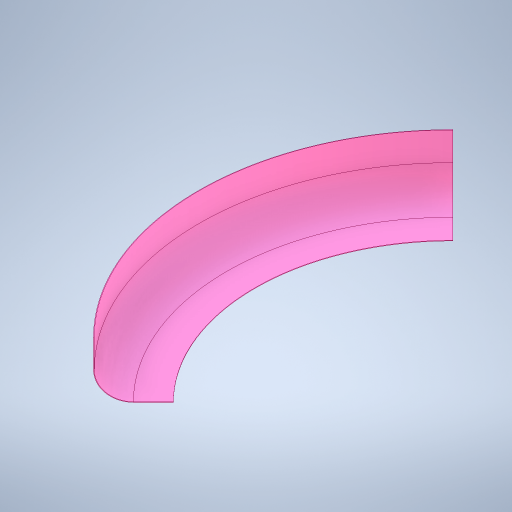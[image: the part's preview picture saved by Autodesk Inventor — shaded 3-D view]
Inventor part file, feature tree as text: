
AUTODESK INVENTOR PART (.ipt)
format: ipt  version: 2023.2 (Build 272271000, 271)  size: 289,792 bytes
history: native  units: mm
features: sketch x2, extrude x1, fillet x1, revolve x1
ambient origin geometry x8: Origin, YZ Plane, XZ Plane, XY Plane, X Axis, Y Axis, Z Axis, Center Point
bodies: Solid1 (feature_tree)
feature tree (5):
  extrude  "Extrusion1"  Depth=500.0mm
  fillet  "Fillet1"  Radius=10.0mm
  revolve  "Revolution1"  [1 undecoded]
  sketch  "Sketch1"  dims[d0=1000.0mm d1=500.0mm d2=10.0mm d3=0.0mm]
  sketch  "Sketch4"  dims[d4=2.0mm d17=500.0mm d18=10.0mm d19=1000.0mm d20=4000.0mm d21=90.0deg]
note: 1 required parameter value undecoded (feature->parameter linkage not recoverable at this tier; creation-order binding heuristic only, values carry confidence <= 0.55)
